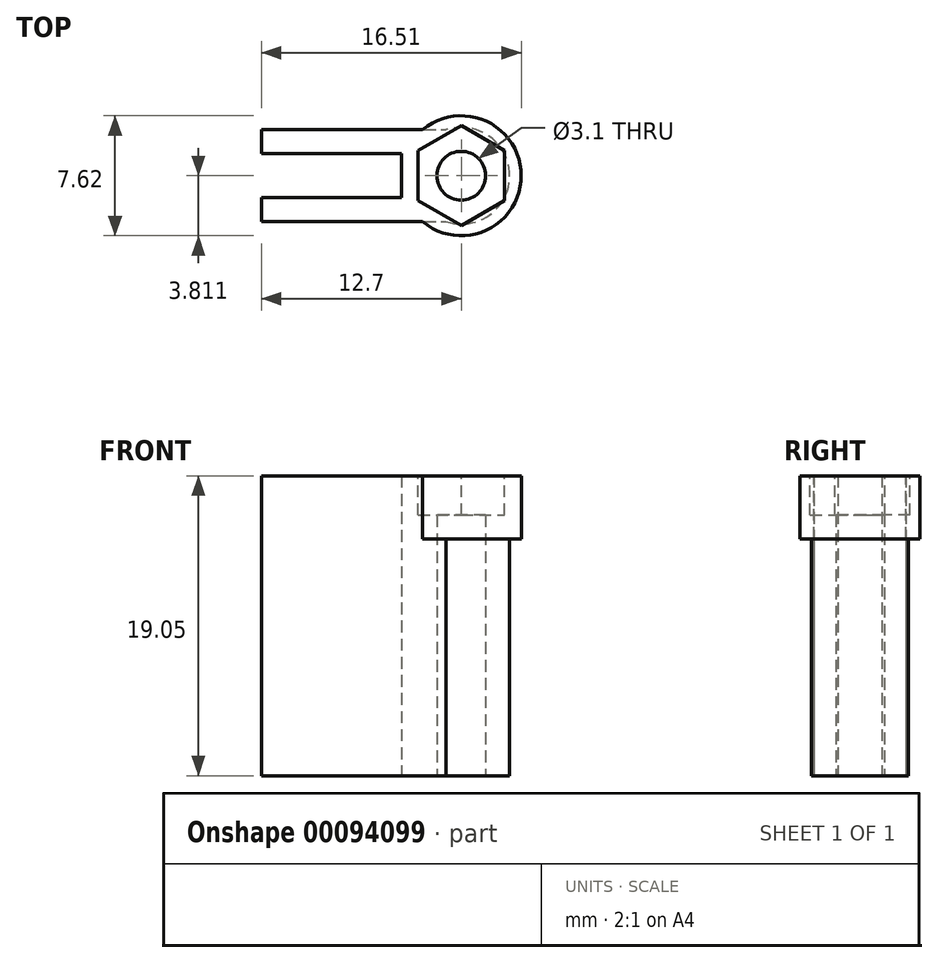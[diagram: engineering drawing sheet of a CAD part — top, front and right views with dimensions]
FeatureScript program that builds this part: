
annotation { "Feature Type Name" : "Feature", "Feature Type Description" : "" }
export const myFeature = defineFeature(function(context is Context, id is Id, definition is map)
    precondition{}
    {
        {
            var Q0;
            Q0=qCreatedBy(makeId("Top.planeOp"),FACE);
            var sketch = newSketch(context, id + "F0", { "sketchPlane" : qUnion([Q0])});
            skLineSegment(sketch, "E0.bottom", {"start": v(0, 0) * mm, "end": v(12.7, 0) * mm});
            skLineSegment(sketch, "E0.top", {"start": v(0, 5.84) * mm, "end": v(12.7, 5.84) * mm});
            skLineSegment(sketch, "E0.left", {"start": v(0, 0) * mm, "end": v(0, 5.84) * mm});
            skLineSegment(sketch, "E0.right", {"start": v(12.7, 0) * mm, "end": v(12.7, 5.84) * mm});
            skLineSegment(sketch, "E1.bottom", {"start": v(0, 4.32) * mm, "end": v(8.9, 4.32) * mm});
            skLineSegment(sketch, "E1.top", {"start": v(0, 1.52) * mm, "end": v(8.9, 1.52) * mm});
            skLineSegment(sketch, "E1.left", {"start": v(0, 4.32) * mm, "end": v(0, 1.52) * mm});
            skLineSegment(sketch, "E1.right", {"start": v(8.9, 4.32) * mm, "end": v(8.9, 1.52) * mm});
            skPoint(sketch, "E2", {"position": v(0, 2.92) * mm});
            skCircle(sketch, "E3", {"center": v(12.7, 2.92) * mm, "radius": 3.07 * mm});
            skCircle(sketch, "E4", {"center": v(12.7, 2.92) * mm, "radius": 1.55 * mm});
            skSolve(sketch);
        }
        {
            var Q0;
            {var subQ0=sQuery(id+"F0.wireOp",EDGE,"E0.right");var subQ7=sQuery(id+"F0.wireOp",EDGE,"E0.bottom");var subQ8=makeQuery(id+"F0.imprint","INTERSECT",VERTEX,{"derivedFrom":[subQ7,subQ0]});Q0=makeQuery(id+"F0.imprint","IMPRINT",FACE,{"disambiguationData":[TD([[makeQuery(id+"F0.imprint","IMPRINT",EDGE,{"disambiguationData":[TD([[subQ8,1.0]])],"derivedFrom":subQ7}),-1.0]])]});}
            var Q1;
            {var subQ8=sQuery(id+"F0.wireOp",EDGE,"E1.right");Q1=makeQuery(id+"F0.imprint","IMPRINT",FACE,{"disambiguationData":[TD([[makeQuery(id+"F0.imprint","IMPRINT",EDGE,{"derivedFrom":subQ8}),1.0]])]});}
            var Q2;
            {var subQ0=sQuery(id+"F0.wireOp",EDGE,"E0.left");var subQ1=sQuery(id+"F0.wireOp",EDGE,"E0.top");var subQ2=makeQuery(id+"F0.imprint","INTERSECT",VERTEX,{"derivedFrom":[subQ1,subQ0]});Q2=makeQuery(id+"F0.imprint","IMPRINT",FACE,{"disambiguationData":[TD([[makeQuery(id+"F0.imprint","IMPRINT",EDGE,{"disambiguationData":[TD([[subQ2,-1.0]])],"derivedFrom":subQ1}),-1.0]])]});}
            var Q3;
            {var subQ0=sQuery(id+"F0.wireOp",EDGE,"E0.left");var subQ1=sQuery(id+"F0.wireOp",EDGE,"E0.bottom");var subQ2=makeQuery(id+"F0.imprint","INTERSECT",VERTEX,{"derivedFrom":[subQ1,subQ0]});Q3=makeQuery(id+"F0.imprint","IMPRINT",FACE,{"disambiguationData":[TD([[makeQuery(id+"F0.imprint","IMPRINT",EDGE,{"disambiguationData":[TD([[subQ2,-1.0]])],"derivedFrom":subQ1}),1.0]])]});}
            var Q4;
            {var subQ0=sQuery(id+"F0.wireOp",EDGE,"E0.right");var subQ7=sQuery(id+"F0.wireOp",EDGE,"E0.bottom");var subQ8=makeQuery(id+"F0.imprint","INTERSECT",VERTEX,{"derivedFrom":[subQ7,subQ0]});Q4=makeQuery(id+"F0.imprint","IMPRINT",FACE,{"disambiguationData":[TD([[makeQuery(id+"F0.imprint","IMPRINT",EDGE,{"disambiguationData":[TD([[subQ8,1.0]])],"derivedFrom":subQ7}),1.0]])]});}
            extrude(context, id + "F1", {"entities" : qUnion([Q0, Q1, Q2, Q3, Q4]), "depth" : 19.05 * mm, "offsetDistance" : 25.4 * mm});
        }
        {
            var Q0;
            Q0=makeQuery(id+"F1.opExtrude","CAP_FACE",FACE,{"disambiguationData":[OSD([sQuery(id+"F0.wireOp",EDGE,"E0.bottom"),sQuery(id+"F0.wireOp",EDGE,"E0.top"),sQuery(id+"F0.wireOp",EDGE,"E0.left"),sQuery(id+"F0.wireOp",EDGE,"E1.bottom"),sQuery(id+"F0.wireOp",EDGE,"E1.top"),sQuery(id+"F0.wireOp",EDGE,"E1.right"),sQuery(id+"F0.wireOp",EDGE,"E3"),sQuery(id+"F0.wireOp",EDGE,"E4")])],"isStart":false});
            var sketch = newSketch(context, id + "F2", { "sketchPlane" : qUnion([Q0])});
            skCircle(sketch, "E5.0", {"center": v(12.7, 2.92) * mm, "radius": 1.55 * mm});
            skCircle(sketch, "E6", {"center": v(12.7, 2.92) * mm, "radius": 3.8 * mm});
            skLineSegment(sketch, "E7.0", {"start": v(8.9, 4.32) * mm, "end": v(8.9, 1.52) * mm});
            skSolve(sketch);
        }
        {
            var Q0;
            {var subQ5=makeQuery(id+"F1.opExtrude","CAP_EDGE",EDGE,{"disambiguationData":[OSD([sQuery(id+"F0.wireOp",EDGE,"E3")])],"isStart":false});Q0=makeQuery(id+"F2.imprint","IMPRINT",FACE,{"disambiguationData":[TD([[makeQuery(id+"F2.imprint","IMPRINT",EDGE,{"derivedFrom":subQ5}),-1.0]])]});}
            extrude(context, id + "F3", {"entities" : qUnion([Q0]), "operationType" : NewBodyOperationType.ADD, "oppositeDirection" : true, "depth" : 4 * mm, "offsetDistance" : 25.4 * mm});
        }
        {
            var Q0;
            Q0=makeQuery(id+"F1.opExtrude","CAP_FACE",FACE,{"disambiguationData":[OSD([sQuery(id+"F0.wireOp",EDGE,"E0.bottom"),sQuery(id+"F0.wireOp",EDGE,"E0.top"),sQuery(id+"F0.wireOp",EDGE,"E0.left"),sQuery(id+"F0.wireOp",EDGE,"E1.bottom"),sQuery(id+"F0.wireOp",EDGE,"E1.top"),sQuery(id+"F0.wireOp",EDGE,"E1.right"),sQuery(id+"F0.wireOp",EDGE,"E3"),sQuery(id+"F0.wireOp",EDGE,"E4")])],"isStart":false});
            var sketch = newSketch(context, id + "F4", { "sketchPlane" : qUnion([Q0])});
            skCircle(sketch, "E8.0", {"center": v(12.7, 2.92) * mm, "radius": 1.55 * mm});
            skCircle(sketch, "E9.cCircle", {"center": v(12.7, 2.92) * mm, "radius": 2.75 * mm, "construction": true});
            skLineSegment(sketch, "E9.0", {"start": v(12.7, 6.1) * mm, "end": v(15.45, 4.5) * mm});
            skLineSegment(sketch, "E9.1", {"start": v(15.45, 4.5) * mm, "end": v(15.45, 1.33) * mm});
            skLineSegment(sketch, "E9.2", {"start": v(15.45, 1.33) * mm, "end": v(12.7, -0.25) * mm});
            skLineSegment(sketch, "E9.3", {"start": v(12.7, -0.25) * mm, "end": v(9.95, 1.33) * mm});
            skLineSegment(sketch, "E9.4", {"start": v(9.95, 1.33) * mm, "end": v(9.95, 4.5) * mm});
            skLineSegment(sketch, "E9.5", {"start": v(9.95, 4.5) * mm, "end": v(12.7, 6.1) * mm});
            skPoint(sketch, "E9.0.midPoint", {"position": v(14.08, 5.3) * mm});
            skLineSegment(sketch, "E10.0", {"start": v(8.9, 4.32) * mm, "end": v(8.9, 1.52) * mm});
            skSolve(sketch);
        }
        {
            var Q0;
            Q0=makeQuery(id+"F4.imprint","IMPRINT",FACE,{"disambiguationData":[TD([[makeQuery(id+"F4.imprint","IMPRINT",EDGE,{"derivedFrom":sQuery(id+"F4.wireOp",EDGE,"E8.0")}),-1.0]])]});
            extrude(context, id + "F5", {"entities" : qUnion([Q0]), "operationType" : NewBodyOperationType.REMOVE, "oppositeDirection" : true, "depth" : 2.5 * mm, "offsetDistance" : 25.4 * mm});
        }
    });
